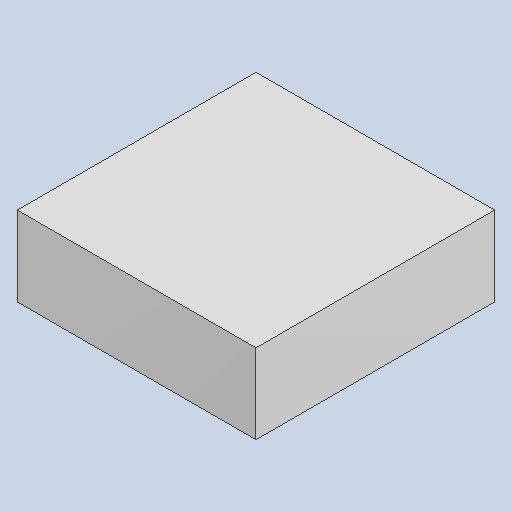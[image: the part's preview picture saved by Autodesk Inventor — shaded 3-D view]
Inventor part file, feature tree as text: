
AUTODESK INVENTOR PART (.ipt)
format: ipt  version: 2023.4 (Build 274418000, 418)  size: 79,872 bytes
history: native  units: mm
features: extrude x1
ambient origin geometry x8: Origin, YZ Plane, XZ Plane, XY Plane, X Axis, Y Axis, Z Axis, Center Point
bodies: Solid1 (feature_tree)
feature tree (1):
  extrude  "Extruded_31"  [1 undecoded]
note: 1 required parameter value undecoded (feature->parameter linkage not recoverable at this tier; creation-order binding heuristic only, values carry confidence <= 0.55)
